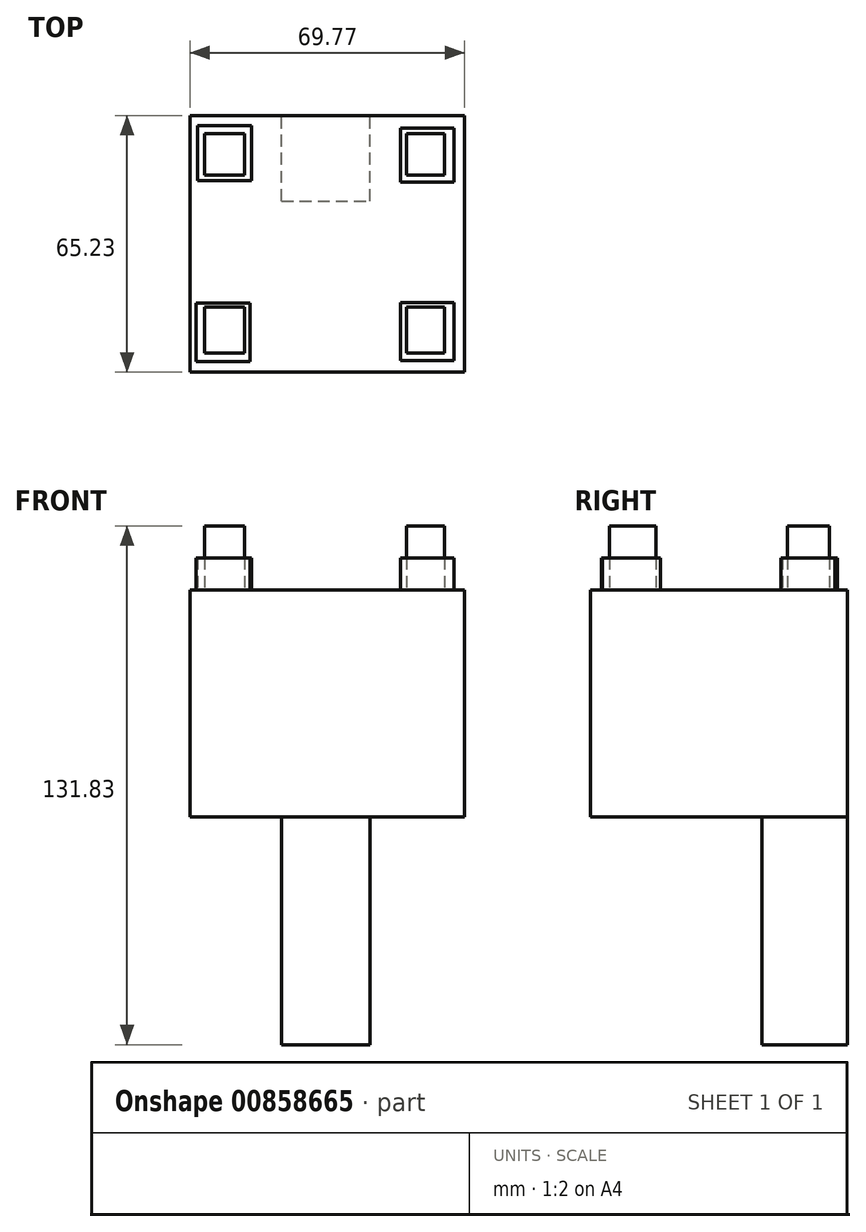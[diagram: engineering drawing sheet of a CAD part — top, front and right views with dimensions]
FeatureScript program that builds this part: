
annotation { "Feature Type Name" : "Feature", "Feature Type Description" : "" }
export const myFeature = defineFeature(function(context is Context, id is Id, definition is map)
    precondition{}
    {
        {
            var Q0;
            Q0=qCreatedBy(makeId("Top.planeOp"),FACE);
            var sketch = newSketch(context, id + "F0", { "sketchPlane" : qUnion([Q0])});
            skLineSegment(sketch, "E0.bottom", {"start": v(0, 0) * mm, "end": v(10.15, 0) * mm});
            skLineSegment(sketch, "E0.top", {"start": v(0, 55.87) * mm, "end": v(10.15, 55.87) * mm});
            skLineSegment(sketch, "E0.left", {"start": v(0, 0) * mm, "end": v(0, 55.87) * mm});
            skLineSegment(sketch, "E0.right", {"start": v(61, 0) * mm, "end": v(61, 11.73) * mm});
            skLineSegment(sketch, "E1.top", {"start": v(0, 45.23) * mm, "end": v(10.15, 45.23) * mm});
            skLineSegment(sketch, "E1.left", {"start": v(0, 55.87) * mm, "end": v(0, 45.23) * mm});
            skLineSegment(sketch, "E1.right", {"start": v(10.15, 55.87) * mm, "end": v(10.15, 45.23) * mm});
            skLineSegment(sketch, "E2.top", {"start": v(0, 11.73) * mm, "end": v(10.15, 11.73) * mm});
            skLineSegment(sketch, "E2.left", {"start": v(0, 0) * mm, "end": v(0, 11.73) * mm});
            skLineSegment(sketch, "E2.right", {"start": v(10.15, 0) * mm, "end": v(10.15, 11.73) * mm});
            skLineSegment(sketch, "E3.bottom", {"start": v(61, 55.87) * mm, "end": v(51.34, 55.87) * mm});
            skLineSegment(sketch, "E3.top", {"start": v(61, 45.23) * mm, "end": v(51.34, 45.23) * mm});
            skLineSegment(sketch, "E3.left", {"start": v(61, 55.87) * mm, "end": v(61, 45.23) * mm});
            skLineSegment(sketch, "E3.right", {"start": v(51.34, 55.87) * mm, "end": v(51.34, 45.23) * mm});
            skLineSegment(sketch, "E4.bottom", {"start": v(61, 0) * mm, "end": v(51.34, 0) * mm});
            skLineSegment(sketch, "E4.top", {"start": v(61, 11.73) * mm, "end": v(51.34, 11.73) * mm});
            skLineSegment(sketch, "E4.right", {"start": v(51.34, 0) * mm, "end": v(51.34, 11.73) * mm});
            skLineSegment(sketch, "E5.trimOffspring", {"start": v(51.34, 55.87) * mm, "end": v(61, 55.87) * mm});
            skLineSegment(sketch, "E6.trimOffspring", {"start": v(61, 45.23) * mm, "end": v(61, 55.87) * mm});
            skLineSegment(sketch, "E7.trimOffspring", {"start": v(51.34, 0) * mm, "end": v(61, 0) * mm});
            skSolve(sketch);
        }
        {
            var Q0;
            Q0=makeQuery(id+"F0.imprint","IMPRINT",FACE,{"disambiguationData":[TD([[makeQuery(id+"F0.imprint","IMPRINT",EDGE,{"derivedFrom":sQuery(id+"F0.wireOp",EDGE,"E0.bottom")}),1.0]])]});
            var Q1;
            Q1=makeQuery(id+"F0.imprint","IMPRINT",FACE,{"disambiguationData":[TD([[makeQuery(id+"F0.imprint","IMPRINT",EDGE,{"derivedFrom":sQuery(id+"F0.wireOp",EDGE,"E4.top")}),1.0]])]});
            var Q2;
            Q2=makeQuery(id+"F0.imprint","IMPRINT",FACE,{"disambiguationData":[TD([[makeQuery(id+"F0.imprint","IMPRINT",EDGE,{"derivedFrom":sQuery(id+"F0.wireOp",EDGE,"E3.top")}),-1.0]])]});
            var Q3;
            Q3=makeQuery(id+"F0.imprint","IMPRINT",FACE,{"disambiguationData":[TD([[makeQuery(id+"F0.imprint","IMPRINT",EDGE,{"derivedFrom":sQuery(id+"F0.wireOp",EDGE,"E0.top")}),-1.0]])]});
            extrude(context, id + "F1", {"entities" : qUnion([Q0, Q1, Q2, Q3]), "depth" : 16.26 * mm, "offsetDistance" : 25.4 * mm});
        }
        {
            var Q0;
            Q0=qCreatedBy(makeId("Top.planeOp"),FACE);
            var sketch = newSketch(context, id + "F2", { "sketchPlane" : qUnion([Q0])});
            skLineSegment(sketch, "E8.bottom", {"start": v(49.76, 57.25) * mm, "end": v(63.36, 57.25) * mm});
            skLineSegment(sketch, "E8.top", {"start": v(49.76, 43.45) * mm, "end": v(63.36, 43.45) * mm});
            skLineSegment(sketch, "E8.left", {"start": v(49.76, 57.25) * mm, "end": v(49.76, 43.45) * mm});
            skLineSegment(sketch, "E8.right", {"start": v(63.36, 57.25) * mm, "end": v(63.36, 43.45) * mm});
            skLineSegment(sketch, "E9.bottom", {"start": v(49.76, 12.9) * mm, "end": v(63.36, 12.9) * mm});
            skLineSegment(sketch, "E9.top", {"start": v(49.76, -1.87) * mm, "end": v(63.36, -1.87) * mm});
            skLineSegment(sketch, "E9.left", {"start": v(49.76, 12.9) * mm, "end": v(49.76, -1.87) * mm});
            skLineSegment(sketch, "E9.right", {"start": v(63.36, 12.9) * mm, "end": v(63.36, -1.87) * mm});
            skLineSegment(sketch, "E10.bottom", {"start": v(-1.68, 57.84) * mm, "end": v(11.92, 57.84) * mm});
            skLineSegment(sketch, "E10.top", {"start": v(-1.68, 43.85) * mm, "end": v(11.92, 43.85) * mm});
            skLineSegment(sketch, "E10.left", {"start": v(-1.68, 57.84) * mm, "end": v(-1.68, 43.85) * mm});
            skLineSegment(sketch, "E10.right", {"start": v(11.92, 57.84) * mm, "end": v(11.92, 43.85) * mm});
            skLineSegment(sketch, "E11.bottom", {"start": v(11.53, 12.71) * mm, "end": v(-2.07, 12.71) * mm});
            skLineSegment(sketch, "E11.top", {"start": v(11.53, -2.07) * mm, "end": v(-2.07, -2.07) * mm});
            skLineSegment(sketch, "E11.left", {"start": v(11.53, 12.71) * mm, "end": v(11.53, -2.07) * mm});
            skLineSegment(sketch, "E11.right", {"start": v(-2.07, 12.71) * mm, "end": v(-2.07, -2.07) * mm});
            skSolve(sketch);
        }
        {
            var Q0;
            Q0=makeQuery(id+"F2.imprint","IMPRINT",FACE,{"disambiguationData":[TD([[makeQuery(id+"F2.imprint","IMPRINT",EDGE,{"derivedFrom":sQuery(id+"F2.wireOp",EDGE,"E8.bottom")}),-1.0]])]});
            var Q1;
            Q1=makeQuery(id+"F2.imprint","IMPRINT",FACE,{"disambiguationData":[TD([[makeQuery(id+"F2.imprint","IMPRINT",EDGE,{"derivedFrom":sQuery(id+"F2.wireOp",EDGE,"E9.bottom")}),-1.0]])]});
            var Q2;
            Q2=makeQuery(id+"F2.imprint","IMPRINT",FACE,{"disambiguationData":[TD([[makeQuery(id+"F2.imprint","IMPRINT",EDGE,{"derivedFrom":sQuery(id+"F2.wireOp",EDGE,"E11.bottom")}),1.0]])]});
            var Q3;
            Q3=makeQuery(id+"F2.imprint","IMPRINT",FACE,{"disambiguationData":[TD([[makeQuery(id+"F2.imprint","IMPRINT",EDGE,{"derivedFrom":sQuery(id+"F2.wireOp",EDGE,"E10.bottom")}),-1.0]])]});
            extrude(context, id + "F3", {"entities" : qUnion([Q0, Q1, Q2, Q3]), "depth" : 8.13 * mm, "offsetDistance" : 25.4 * mm});
        }
        {
            var Q0;
            Q0=qCreatedBy(makeId("Top.planeOp"),FACE);
            var sketch = newSketch(context, id + "F4", { "sketchPlane" : qUnion([Q0])});
            skLineSegment(sketch, "E12.bottom", {"start": v(-3.65, -4.83) * mm, "end": v(66.12, -4.83) * mm});
            skLineSegment(sketch, "E12.top", {"start": v(-3.65, 60.4) * mm, "end": v(66.12, 60.4) * mm});
            skLineSegment(sketch, "E12.left", {"start": v(-3.65, -4.83) * mm, "end": v(-3.65, 60.4) * mm});
            skLineSegment(sketch, "E12.right", {"start": v(66.12, -4.83) * mm, "end": v(66.12, 60.4) * mm});
            skSolve(sketch);
        }
        {
            var Q0;
            Q0=makeQuery(id+"F4.imprint","IMPRINT",FACE,{"disambiguationData":[TD([[makeQuery(id+"F4.imprint","IMPRINT",EDGE,{"derivedFrom":sQuery(id+"F4.wireOp",EDGE,"E12.bottom")}),1.0]])]});
            extrude(context, id + "F5", {"entities" : qUnion([Q0]), "oppositeDirection" : true, "depth" : 57.66 * mm, "offsetDistance" : 25.4 * mm});
        }
        {
            var Q0;
            Q0=qCreatedBy(makeId("Top.planeOp"),FACE);
            var sketch = newSketch(context, id + "F6", { "sketchPlane" : qUnion([Q0])});
            skLineSegment(sketch, "E13.bottom", {"start": v(19.6, 38.72) * mm, "end": v(42.07, 38.72) * mm});
            skLineSegment(sketch, "E13.top", {"start": v(19.6, 60.4) * mm, "end": v(42.07, 60.4) * mm});
            skLineSegment(sketch, "E13.left", {"start": v(19.6, 38.72) * mm, "end": v(19.6, 60.4) * mm});
            skLineSegment(sketch, "E13.right", {"start": v(42.07, 38.72) * mm, "end": v(42.07, 60.4) * mm});
            skSolve(sketch);
        }
        {
            var Q0;
            Q0=makeQuery(id+"F6.imprint","IMPRINT",FACE,{"disambiguationData":[TD([[makeQuery(id+"F6.imprint","IMPRINT",EDGE,{"derivedFrom":sQuery(id+"F6.wireOp",EDGE,"E13.bottom")}),1.0]])]});
            extrude(context, id + "F7", {"entities" : qUnion([Q0]), "operationType" : NewBodyOperationType.ADD, "oppositeDirection" : true, "depth" : 115.57 * mm, "offsetDistance" : 25.4 * mm});
        }
    });
